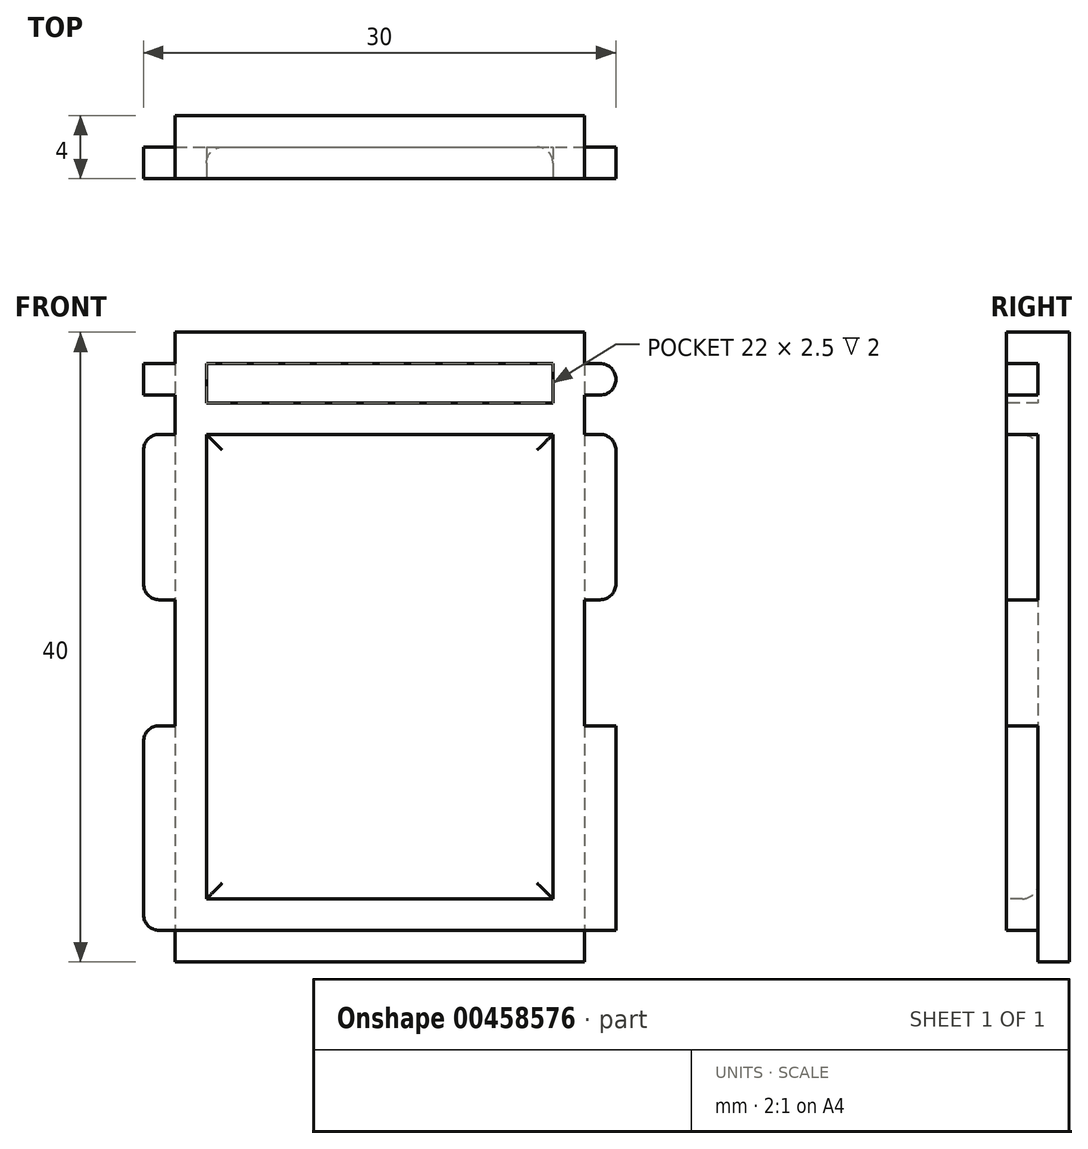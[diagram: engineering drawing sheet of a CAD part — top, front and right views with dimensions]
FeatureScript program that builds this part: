
annotation { "Feature Type Name" : "Feature", "Feature Type Description" : "" }
export const myFeature = defineFeature(function(context is Context, id is Id, definition is map)
    precondition{}
    {
        {
            var Q0;
            Q0=qCreatedBy(makeId("Front.planeOp"),FACE);
            var sketch = newSketch(context, id + "F0", { "sketchPlane" : qUnion([Q0])});
            skLineSegment(sketch, "E0.bottom", {"start": v(-13.06, 25.03) * mm, "end": v(12.94, 25.03) * mm});
            skLineSegment(sketch, "E0.top", {"start": v(-13.06, -14.97) * mm, "end": v(12.94, -14.97) * mm});
            skLineSegment(sketch, "E0.left", {"start": v(-13.06, 25.03) * mm, "end": v(-13.06, -14.97) * mm});
            skLineSegment(sketch, "E0.right", {"start": v(12.94, 25.03) * mm, "end": v(12.94, -14.97) * mm});
            skSolve(sketch);
        }
        {
            var Q0;
            Q0 = qSketchRegion(id + "F0", true);
            extrude(context, id + "F1", {"entities" : qUnion([Q0]), "depth" : 2 * mm, "offsetDistance" : 25 * mm});
        }
        {
            var Q0;
            Q0=makeQuery(id+"F1.opExtrude","CAP_FACE",FACE,{"disambiguationData":[OSD([sQuery(id+"F0.wireOp",EDGE,"E0.bottom"),sQuery(id+"F0.wireOp",EDGE,"E0.top"),sQuery(id+"F0.wireOp",EDGE,"E0.left"),sQuery(id+"F0.wireOp",EDGE,"E0.right")])],"isStart":false});
            var sketch = newSketch(context, id + "F2", { "sketchPlane" : qUnion([Q0])});
            skLineSegment(sketch, "E1.bottom", {"start": v(-15.06, 25.03) * mm, "end": v(14.94, 25.03) * mm});
            skLineSegment(sketch, "E1.top", {"start": v(-15.06, -14.97) * mm, "end": v(14.94, -14.97) * mm});
            skLineSegment(sketch, "E1.left", {"start": v(-15.06, 25.03) * mm, "end": v(-15.06, -14.97) * mm});
            skLineSegment(sketch, "E1.right", {"start": v(14.94, 25.03) * mm, "end": v(14.94, -14.97) * mm});
            skPoint(sketch, "E1.middle", {"position": v(-0.06, 5.03) * mm});
            skSolve(sketch);
        }
        {
            var Q0;
            Q0 = qSketchRegion(id + "F2", true);
            extrude(context, id + "F3", {"entities" : qUnion([Q0]), "operationType" : NewBodyOperationType.ADD, "depth" : 2 * mm, "offsetDistance" : 25 * mm});
        }
        {
            var Q0;
            Q0=makeQuery(id+"F3.opExtrude","CAP_FACE",FACE,{"disambiguationData":[OSD([sQuery(id+"F2.wireOp",EDGE,"E1.bottom"),sQuery(id+"F2.wireOp",EDGE,"E1.top"),sQuery(id+"F2.wireOp",EDGE,"E1.left"),sQuery(id+"F2.wireOp",EDGE,"E1.right")])],"isStart":false});
            var sketch = newSketch(context, id + "F4", { "sketchPlane" : qUnion([Q0])});
            skLineSegment(sketch, "E2.bottom", {"start": v(-15.06, 25.03) * mm, "end": v(-13.06, 25.03) * mm});
            skLineSegment(sketch, "E2.top", {"start": v(-15.06, 23.03) * mm, "end": v(-13.06, 23.03) * mm});
            skLineSegment(sketch, "E2.left", {"start": v(-15.06, 25.03) * mm, "end": v(-15.06, 23.03) * mm});
            skLineSegment(sketch, "E2.right", {"start": v(-13.06, 25.03) * mm, "end": v(-13.06, 23.03) * mm});
            skLineSegment(sketch, "E3.bottom", {"start": v(14.94, 25.03) * mm, "end": v(12.94, 25.03) * mm});
            skLineSegment(sketch, "E3.top", {"start": v(14.94, 23.03) * mm, "end": v(12.94, 23.03) * mm});
            skLineSegment(sketch, "E3.left", {"start": v(14.94, 25.03) * mm, "end": v(14.94, 23.03) * mm});
            skLineSegment(sketch, "E3.right", {"start": v(12.94, 25.03) * mm, "end": v(12.94, 23.03) * mm});
            skLineSegment(sketch, "E4.bottom", {"start": v(-15.06, 21.03) * mm, "end": v(-13.06, 21.03) * mm});
            skLineSegment(sketch, "E4.top", {"start": v(-15.06, 18.53) * mm, "end": v(-13.06, 18.53) * mm});
            skLineSegment(sketch, "E4.left", {"start": v(-15.06, 21.03) * mm, "end": v(-15.06, 18.53) * mm});
            skLineSegment(sketch, "E4.right", {"start": v(-13.06, 21.03) * mm, "end": v(-13.06, 18.53) * mm});
            skLineSegment(sketch, "E5.bottom", {"start": v(14.94, 21.03) * mm, "end": v(12.94, 21.03) * mm});
            skLineSegment(sketch, "E5.top", {"start": v(14.94, 18.53) * mm, "end": v(12.94, 18.53) * mm});
            skLineSegment(sketch, "E5.left", {"start": v(14.94, 21.03) * mm, "end": v(14.94, 18.53) * mm});
            skLineSegment(sketch, "E5.right", {"start": v(12.94, 21.03) * mm, "end": v(12.94, 18.53) * mm});
            skLineSegment(sketch, "E6.bottom", {"start": v(-15.06, -14.97) * mm, "end": v(14.94, -14.97) * mm});
            skLineSegment(sketch, "E6.top", {"start": v(-15.06, -12.97) * mm, "end": v(14.94, -12.97) * mm});
            skLineSegment(sketch, "E6.left", {"start": v(-15.06, -14.97) * mm, "end": v(-15.06, -12.97) * mm});
            skLineSegment(sketch, "E6.right", {"start": v(14.94, -14.97) * mm, "end": v(14.94, -12.97) * mm});
            skLineSegment(sketch, "E7.bottom", {"start": v(-11.06, 23.03) * mm, "end": v(10.94, 23.03) * mm});
            skLineSegment(sketch, "E7.top", {"start": v(-11.06, 20.53) * mm, "end": v(10.94, 20.53) * mm});
            skLineSegment(sketch, "E7.left", {"start": v(-11.06, 23.03) * mm, "end": v(-11.06, 20.53) * mm});
            skLineSegment(sketch, "E7.right", {"start": v(10.94, 23.03) * mm, "end": v(10.94, 20.53) * mm});
            skLineSegment(sketch, "E8.bottom", {"start": v(-15.06, 8.03) * mm, "end": v(-13.06, 8.03) * mm});
            skLineSegment(sketch, "E8.top", {"start": v(-15.06, 0.03) * mm, "end": v(-13.06, 0.03) * mm});
            skLineSegment(sketch, "E8.left", {"start": v(-15.06, 8.03) * mm, "end": v(-15.06, 0.03) * mm});
            skLineSegment(sketch, "E8.right", {"start": v(-13.06, 8.03) * mm, "end": v(-13.06, 0.03) * mm});
            skLineSegment(sketch, "E9.bottom", {"start": v(14.94, 8.03) * mm, "end": v(12.94, 8.03) * mm});
            skLineSegment(sketch, "E9.top", {"start": v(14.94, 0.03) * mm, "end": v(12.94, 0.03) * mm});
            skLineSegment(sketch, "E9.left", {"start": v(14.94, 8.03) * mm, "end": v(14.94, 0.03) * mm});
            skLineSegment(sketch, "E9.right", {"start": v(12.94, 8.03) * mm, "end": v(12.94, 0.03) * mm});
            skLineSegment(sketch, "E10.bottom", {"start": v(-11.06, 18.53) * mm, "end": v(10.94, 18.53) * mm});
            skLineSegment(sketch, "E10.top", {"start": v(-11.06, -10.97) * mm, "end": v(10.94, -10.97) * mm});
            skLineSegment(sketch, "E10.left", {"start": v(-11.06, 18.53) * mm, "end": v(-11.06, -10.97) * mm});
            skLineSegment(sketch, "E10.right", {"start": v(10.94, 18.53) * mm, "end": v(10.94, -10.97) * mm});
            skSolve(sketch);
        }
        {
            var Q0;
            Q0 = qSketchRegion(id + "F4", true);
            extrude(context, id + "F5", {"entities" : qUnion([Q0]), "operationType" : NewBodyOperationType.REMOVE, "oppositeDirection" : true, "depth" : 2 * mm, "offsetDistance" : 25 * mm});
        }
        {
            var Q0;
            Q0=makeQuery(id+"F5.boolean.opBoolean","COPY",EDGE,{"derivedFrom":makeQuery(id+"F5.opExtrude","SWEPT_EDGE",EDGE,{"disambiguationData":[OSD([sQuery(id+"F2.wireOp",EDGE,"E1.right"),sQuery(id+"F4.wireOp",EDGE,"E3.top"),sQuery(id+"F4.wireOp",EDGE,"E3.left")])]})});
            var Q1;
            Q1=makeQuery(id+"F5.boolean.opBoolean","COPY",EDGE,{"derivedFrom":makeQuery(id+"F5.opExtrude","SWEPT_EDGE",EDGE,{"disambiguationData":[OSD([sQuery(id+"F2.wireOp",EDGE,"E1.right"),sQuery(id+"F4.wireOp",EDGE,"E5.bottom"),sQuery(id+"F4.wireOp",EDGE,"E5.left")])]})});
            var Q2;
            Q2=makeQuery(id+"F5.boolean.opBoolean","COPY",EDGE,{"derivedFrom":makeQuery(id+"F5.opExtrude","SWEPT_EDGE",EDGE,{"disambiguationData":[OSD([sQuery(id+"F2.wireOp",EDGE,"E1.right"),sQuery(id+"F4.wireOp",EDGE,"E5.top"),sQuery(id+"F4.wireOp",EDGE,"E5.left")])]})});
            var Q3;
            Q3=makeQuery(id+"F5.boolean.opBoolean","COPY",EDGE,{"derivedFrom":makeQuery(id+"F5.opExtrude","SWEPT_EDGE",EDGE,{"disambiguationData":[OSD([sQuery(id+"F2.wireOp",EDGE,"E1.right"),sQuery(id+"F4.wireOp",EDGE,"E6.top"),sQuery(id+"F4.wireOp",EDGE,"E6.right")])]})});
            var Q4;
            Q4=makeQuery(id+"F5.boolean.opBoolean","COPY",EDGE,{"derivedFrom":makeQuery(id+"F5.opExtrude","SWEPT_EDGE",EDGE,{"disambiguationData":[OSD([sQuery(id+"F2.wireOp",EDGE,"E1.left"),sQuery(id+"F4.wireOp",EDGE,"E6.top"),sQuery(id+"F4.wireOp",EDGE,"E6.left")])]})});
            var Q5;
            Q5=makeQuery(id+"F5.boolean.opBoolean","COPY",EDGE,{"derivedFrom":makeQuery(id+"F5.opExtrude","SWEPT_EDGE",EDGE,{"disambiguationData":[OSD([sQuery(id+"F2.wireOp",EDGE,"E1.left"),sQuery(id+"F4.wireOp",EDGE,"E4.top"),sQuery(id+"F4.wireOp",EDGE,"E4.left")])]})});
            var Q6;
            Q6=makeQuery(id+"F5.boolean.opBoolean","COPY",EDGE,{"derivedFrom":makeQuery(id+"F5.opExtrude","SWEPT_EDGE",EDGE,{"disambiguationData":[OSD([sQuery(id+"F2.wireOp",EDGE,"E1.left"),sQuery(id+"F4.wireOp",EDGE,"E2.top"),sQuery(id+"F4.wireOp",EDGE,"E2.left")])]})});
            var Q7;
            Q7=makeQuery(id+"F5.boolean.opBoolean","COPY",EDGE,{"derivedFrom":makeQuery(id+"F5.opExtrude","SWEPT_EDGE",EDGE,{"disambiguationData":[OSD([sQuery(id+"F2.wireOp",EDGE,"E1.left"),sQuery(id+"F4.wireOp",EDGE,"E4.bottom"),sQuery(id+"F4.wireOp",EDGE,"E4.left")])]})});
            var Q8;
            Q8=makeQuery(id+"F5.boolean.opBoolean","COPY",EDGE,{"derivedFrom":makeQuery(id+"F5.opExtrude","SWEPT_EDGE",EDGE,{"disambiguationData":[OSD([sQuery(id+"F2.wireOp",EDGE,"E1.left"),sQuery(id+"F4.wireOp",EDGE,"E8.bottom"),sQuery(id+"F4.wireOp",EDGE,"E8.left")])]})});
            var Q9;
            Q9=makeQuery(id+"F5.boolean.opBoolean","COPY",EDGE,{"derivedFrom":makeQuery(id+"F5.opExtrude","SWEPT_EDGE",EDGE,{"disambiguationData":[OSD([sQuery(id+"F2.wireOp",EDGE,"E1.left"),sQuery(id+"F4.wireOp",EDGE,"E8.top"),sQuery(id+"F4.wireOp",EDGE,"E8.left")])]})});
            var Q10;
            Q10=makeQuery(id+"F5.boolean.opBoolean","COPY",EDGE,{"derivedFrom":makeQuery(id+"F5.opExtrude","SWEPT_EDGE",EDGE,{"disambiguationData":[OSD([sQuery(id+"F2.wireOp",EDGE,"E1.right"),sQuery(id+"F4.wireOp",EDGE,"E9.bottom"),sQuery(id+"F4.wireOp",EDGE,"E9.left")])]})});
            var Q11;
            Q11=makeQuery(id+"F5.boolean.opBoolean","COPY",EDGE,{"derivedFrom":makeQuery(id+"F5.opExtrude","SWEPT_EDGE",EDGE,{"disambiguationData":[OSD([sQuery(id+"F2.wireOp",EDGE,"E1.right"),sQuery(id+"F4.wireOp",EDGE,"E9.top"),sQuery(id+"F4.wireOp",EDGE,"E9.left")])]})});
            var Q12;
            Q12=makeQuery(id+"F5.boolean.opBoolean","COPY",FACE,{"derivedFrom":makeQuery(id+"F5.opExtrude","CAP_FACE",FACE,{"disambiguationData":[OSD([sQuery(id+"F4.wireOp",EDGE,"E10.bottom"),sQuery(id+"F4.wireOp",EDGE,"E10.top"),sQuery(id+"F4.wireOp",EDGE,"E10.left"),sQuery(id+"F4.wireOp",EDGE,"E10.right")])],"isStart":false})});
            var Q13;
            Q13=makeQuery(id+"F5.boolean.opBoolean","COPY",EDGE,{"derivedFrom":makeQuery(id+"F5.opExtrude","CAP_EDGE",EDGE,{"disambiguationData":[OSD([sQuery(id+"F4.wireOp",EDGE,"E10.bottom")])],"isStart":true})});
            var Q14;
            Q14=makeQuery(id+"F5.boolean.opBoolean","COPY",EDGE,{"derivedFrom":makeQuery(id+"F5.opExtrude","CAP_EDGE",EDGE,{"disambiguationData":[OSD([sQuery(id+"F4.wireOp",EDGE,"E10.left")])],"isStart":true})});
            var Q15;
            Q15=makeQuery(id+"F5.boolean.opBoolean","COPY",EDGE,{"derivedFrom":makeQuery(id+"F5.opExtrude","CAP_EDGE",EDGE,{"disambiguationData":[OSD([sQuery(id+"F4.wireOp",EDGE,"E10.top")])],"isStart":true})});
            var Q16;
            Q16=makeQuery(id+"F5.boolean.opBoolean","COPY",EDGE,{"derivedFrom":makeQuery(id+"F5.opExtrude","CAP_EDGE",EDGE,{"disambiguationData":[OSD([sQuery(id+"F4.wireOp",EDGE,"E10.right")])],"isStart":true})});
            fillet(context, id + "F6", {"entities" : qUnion([Q0, Q1, Q2, Q3, Q4, Q5, Q6, Q7, Q8, Q9, Q10, Q11, Q12, Q13, Q14, Q15, Q16]), "radius" : 1 * mm, "tangentPropagation" : true, "allowEdgeOverflow" : false});
        }
    });
